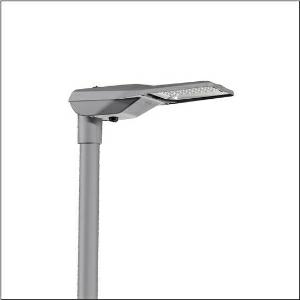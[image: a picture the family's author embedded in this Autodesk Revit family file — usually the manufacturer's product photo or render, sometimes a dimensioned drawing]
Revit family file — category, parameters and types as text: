
# Revit family: streetlight_sl_21_iq_mini___stw1_0a_5xe2e31y08hb_518f
name_source: partatom
category: Lighting Fixtures
units: mm (PartAtom-declared; Revit-internal decimal feet)

## family parameters
Cut with Voids When Loaded = No
Host = Face
Light Source = No
Part Type = Normal
Room Calculation Point = No
Round Connector Dimension = Use Diameter
Shared = No

## types (1)
- --- (1 x LED, 9750 lm, 71 W, 3000K)
    Apparent Load = 71 VA
    CIE Flux Codes = 38 75 98 100 100
    Color Rendering = 70
    Color Temperature = 3000K
    Default Elevation = 1800 mm
    Description = Streetlight SL 21 iQ mini, mast luminaire, primary light control with lens, of PMMA, primary optical cover: cover, of toughened safety glass, transparent, light distribution: STW1.0a, light emission: direct distribution, primary light characteristic: asymmetric, installation type: post-top, side-entry, LED, High Power LED, rated luminous flux: 9.750lm, luminous efficacy: 137lm/W, light colour: 730, colour temperature: 3000K, control gear: iQ-Street Remote, D4i with power reduction, control: pre-setting: logarithmic dimming characteristic, Street-Remote, Auto-Match, Temp-Guard, Lumen-Switch, Night-Set, Smart-Wire, Light-Fading, Desk-Remote (wireless, voltage-free reading and setting of iQ features in the workshop via application-optimized NFC function/RFID function), optimised constant luminous flux control (CLO 2.0), mains connection: 220..240V, AC, 50/60Hz, start of lifetime: 71W, end of service life: 75W, reduction: 30W, luminaire housing, of diecast aluminium, powder-coated, Siteco® metallic grey (DB 702S), corrosivity category C5 mid according to DIN EN ISO 12944, please order mast flange separately, inclination adjustable: 0°, 5°, 10°, 15°, sealing non-destructively replaceable, multi-level sealing system, length: 628mm, width: 235mm, height: 110mm, mast flange for spigot size: 42mm (side-entry): 5XC10008XM4, 60/48mm (side-entry/post-top): 5XC10108XM2, 76/60mm (side-entry/post-top): 5XC10108XM1, mounting height: 4..8m, Smart Interface below and above, protection rating (complete): IP66, insulation class (complete): insulation class II (safety insulation), certification: CE, ENEC, ENEC+, VDE, impact resistance: IK10, permissible operating ambient temperature for outdoor applications: -40..+50°C, standard-compliant lighting for roads and squares, packaging unit: 1 piece

Light Distribution: STW1.0a
    Height = 110 mm
    Lamp = 1 x LED
    Lamp Light Flux = 9750 lm
    Lamp Power = 71 W
    Lamp count = 1
    Length = 625 mm
    Luminous efficacy = 137 lm/W
    Manufacturer = Siteco
    ModVariant = No
    Model = 5XE2E31Y08HB
    Number of Poles = 1
    OnlyDefault = Yes
    Power Factor = 1
    Product Name = Streetlight SL 21 iQ mini | STW1.0a
    Product group = mast luminaire | pylon top
    ProductGroupID = 6100
    Protection Class = Protection class II
    Protection Degree = IP 66
    RLX_Detail_Level = 1
    RLX_Emergency_Light_Flux = 0 lm
    RLX_Emergency_Type = 0
    RLX_Emergency_Type_DB = No
    RlxData = <blob elided: 92417 chars, md5=3a2ea911>
    Socket = socket
    Standby Power = 0 W
    System Light Flux = 9750 lm
    System Power = 71 W
    Type Comments = factory setting: luminous flux: 100 % | dim-lin: 254 | 716 mA
    Type Image = l_1003514.jpg
    URL = http://relux.com
    VarID = @adj_135777
    Voltage = 0 V
    Weight = 0.00 kg
    Width = 234 mm

## geometry (parser evidence)
native form markers: Blend x4, Sweep x14
no freeform markers — native parametric forms only
